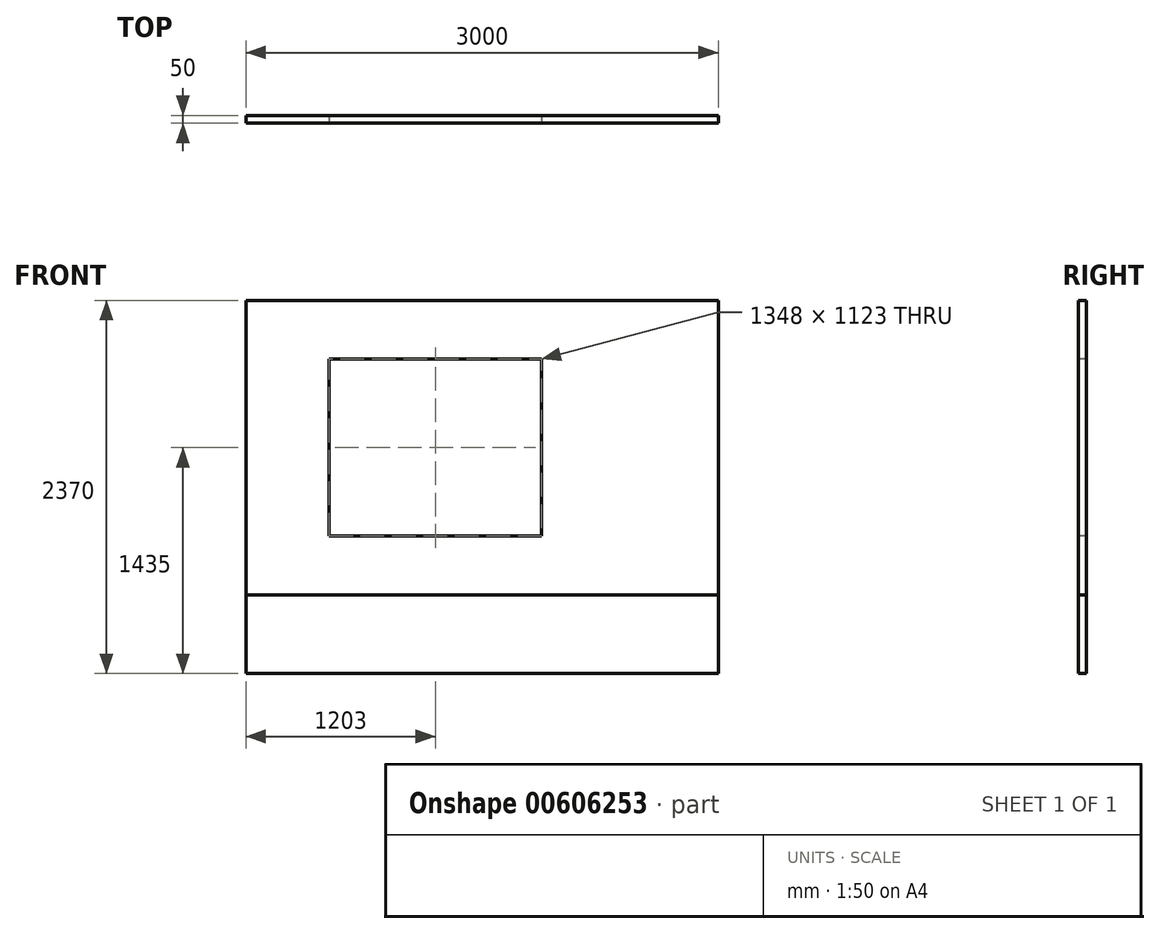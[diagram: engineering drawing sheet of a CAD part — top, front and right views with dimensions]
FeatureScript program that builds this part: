
annotation { "Feature Type Name" : "Feature", "Feature Type Description" : "" }
export const myFeature = defineFeature(function(context is Context, id is Id, definition is map)
    precondition{}
    {
        {
            var Q0;
            Q0=qCreatedBy(makeId("Front.planeOp"),FACE);
            var sketch = newSketch(context, id + "F0", { "sketchPlane" : qUnion([Q0])});
            skLineSegment(sketch, "E0.bottom", {"start": v(1500, -935) * mm, "end": v(-1500, -935) * mm});
            skLineSegment(sketch, "E0.top", {"start": v(1500, 935) * mm, "end": v(-1500, 935) * mm});
            skLineSegment(sketch, "E0.left", {"start": v(1500, -935) * mm, "end": v(1500, 935) * mm});
            skLineSegment(sketch, "E0.right", {"start": v(-1500, -935) * mm, "end": v(-1500, 935) * mm});
            skPoint(sketch, "E0.middle", {"position": v(0, 0) * mm});
            skSolve(sketch);
        }
        {
            var Q0;
            Q0=makeQuery(id+"F0.imprint","IMPRINT",FACE,{"disambiguationData":[TD([[makeQuery(id+"F0.imprint","IMPRINT",EDGE,{"derivedFrom":sQuery(id+"F0.wireOp",EDGE,"E0.bottom")}),-1.0]])]});
            extrude(context, id + "F1", {"entities" : qUnion([Q0]), "depth" : 50 * mm, "offsetDistance" : 25 * mm});
        }
        {
            var Q0;
            Q0=makeQuery(id+"F1.opExtrude","CAP_FACE",FACE,{"disambiguationData":[OSD([sQuery(id+"F0.wireOp",EDGE,"E0.bottom"),sQuery(id+"F0.wireOp",EDGE,"E0.top"),sQuery(id+"F0.wireOp",EDGE,"E0.left"),sQuery(id+"F0.wireOp",EDGE,"E0.right")])],"isStart":false});
            var sketch = newSketch(context, id + "F2", { "sketchPlane" : qUnion([Q0])});
            skLineSegment(sketch, "E1.bottom", {"start": v(-971, 561.5) * mm, "end": v(377, 561.5) * mm});
            skLineSegment(sketch, "E1.top", {"start": v(-971, -561.5) * mm, "end": v(377, -561.5) * mm});
            skLineSegment(sketch, "E1.left", {"start": v(-971, 561.5) * mm, "end": v(-971, -561.5) * mm});
            skLineSegment(sketch, "E1.right", {"start": v(377, 561.5) * mm, "end": v(377, -561.5) * mm});
            skSolve(sketch);
        }
        {
            var Q0;
            Q0=qSketchRegion(id+"F2",true);
            extrude(context, id + "F3", {"entities" : qUnion([Q0]), "operationType" : NewBodyOperationType.REMOVE, "endBound" : BoundingType.UP_TO_NEXT, "oppositeDirection" : true, "depth" : 25 * mm, "offsetDistance" : 25 * mm});
        }
        {
            var Q0;
            Q0=makeQuery(id+"F1.opExtrude","SWEPT_FACE",FACE,{"disambiguationData":[OSD([sQuery(id+"F0.wireOp",EDGE,"E0.bottom")])]});
            extrude(context, id + "F4", {"entities" : qUnion([Q0]), "depth" : 500 * mm, "offsetDistance" : 25 * mm});
        }
    });
